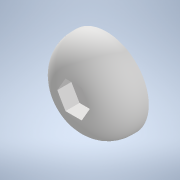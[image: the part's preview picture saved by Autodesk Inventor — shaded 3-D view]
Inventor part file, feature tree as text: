
AUTODESK INVENTOR PART (.ipt)
format: ipt  version: 2022 (Build 260153070, 153G)  size: 141,824 bytes
history: native  units: in
note: dims shown in document units (in); Inventor stores cm internally (conversion verified against a paired STEP export)
features: extrude x2, sketch x2, fillet x1
ambient origin geometry x8: Origin, YZ Plane, XZ Plane, XY Plane, X Axis, Y Axis, Z Axis, Center Point
bodies: Solid1 (feature_tree)
feature tree (5):
  extrude  "Extrusion1"  Depth=0.1181in TaperAngle=0.0deg
  fillet  "Fillet1"  Radius=0.1181in
  extrude  "Extrusion2"  Depth=0.1181in TaperAngle=0.0deg
  sketch  "Sketch1"  dims[d0=0.3543in d1=0.1378in d2=0.0in d3=0.1181in]
  sketch  "Sketch2"  dims[d4=0.1181in d5=0.0591in d6=0.0in]
